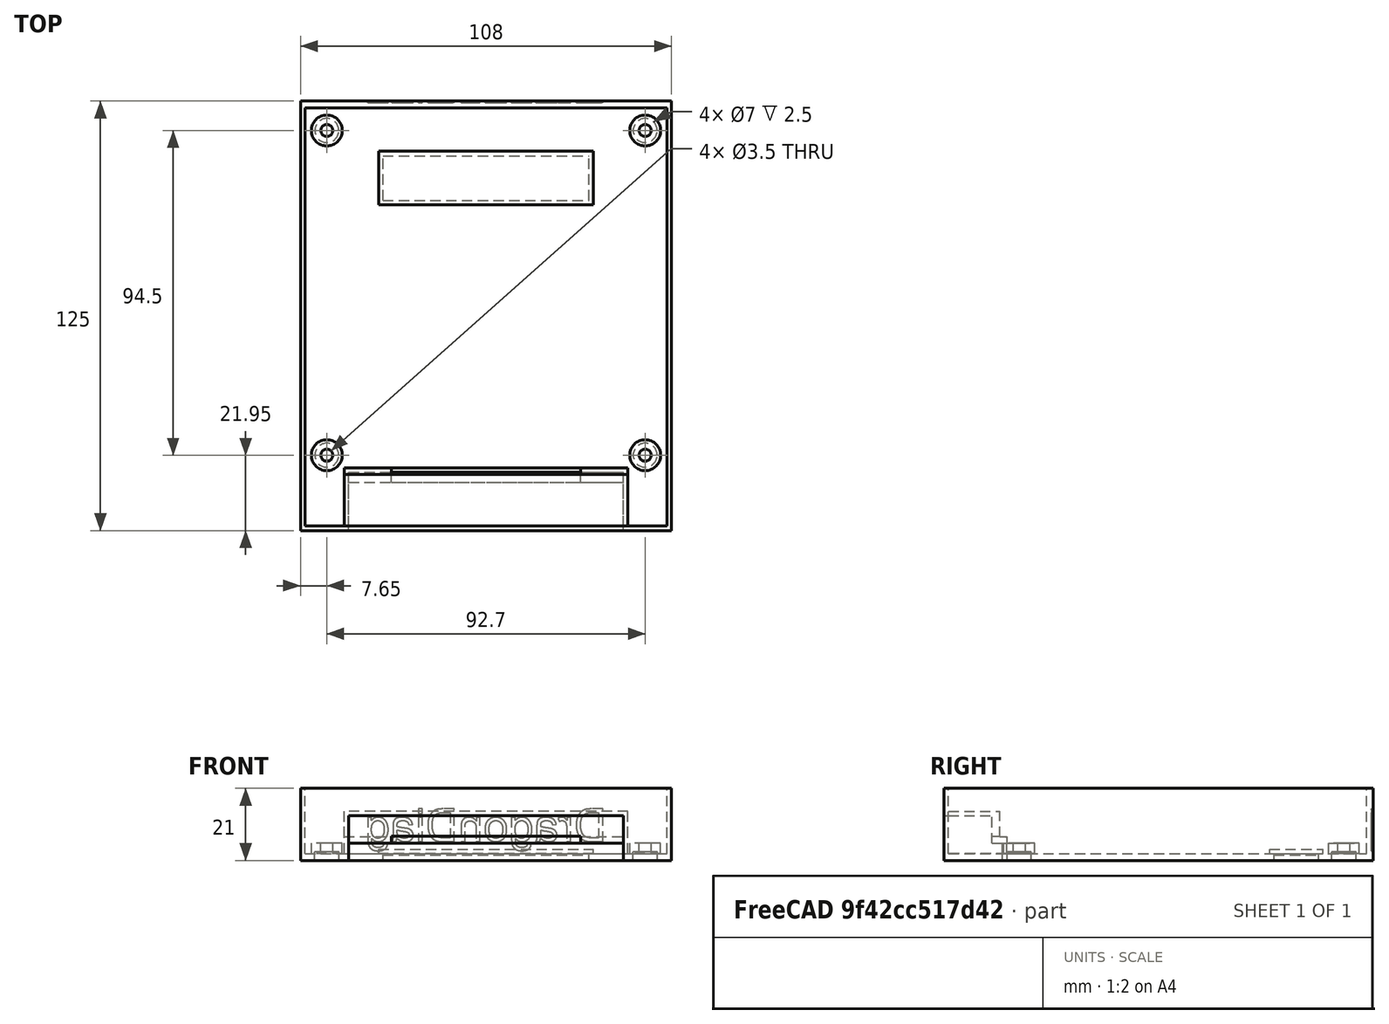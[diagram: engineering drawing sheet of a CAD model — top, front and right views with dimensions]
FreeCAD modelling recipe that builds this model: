
FCSTD DOCUMENT  (FreeCAD 0.18R4 (GitTag))
Label: DragonDiagBottom-v3
License: All rights reserved
LicenseURL: http://en.wikipedia.org/wiki/All_rights_reserved
objects: Part::Box×10, Part::Cut×9, Part::Cylinder×6, Part::MultiFuse×5, Part::FeaturePython×3, Part::Part2DObjectPython×1, Part::Extrusion×1
note: 35 computed .brp shape members not serialized (recipe doc carries the construction recipe); baked Part::Feature solids carry a one-line shape summary decoded from their .brp

FEATURE [Part::Box] Box  label="Cube"
  AttacherType = Attacher::AttachEngine3D
  Height = 21
  Length = 108
  Width = 125
FEATURE [Part::Box] Box001  label="Cube001"
  AttacherType = Attacher::AttachEngine3D
  Height = 19
  Length = 105.4
  Placement = pos=(1.3,1.3,2) rot=(0,0,1;0rad)
  Width = 121.7
FEATURE [Part::Cut] Cut  label="Outer Box"
  Base = -> Box
  Tool = -> Box001
FEATURE [Part::Box] Box002  label="Cube002"
  AttacherType = Attacher::AttachEngine3D
  Height = 13
  Length = 80
  Placement = pos=(14,0,0) rot=(0,0,1;0rad)
  Width = 17
FEATURE [Part::Cut] Cut001  label="Cartridge appature cutout"
  Base = -> Cut
  Tool = -> Box002
FEATURE [Part::Box] Box003  label="Appature"
  AttacherType = Attacher::AttachEngine3D
  Height = 14.3
  Length = 82.6
  Placement = pos=(12.7,0,0) rot=(0,0,1;0rad)
  Width = 18.3
FEATURE [Part::Box] Box004  label="Appature bottom outside carve"
  AttacherType = Attacher::AttachEngine3D
  Height = 5
  Length = 80
  Placement = pos=(14,0,0) rot=(0,0,1;0rad)
  Width = 17
FEATURE [Part::Cut] Cut002  label="AppatureC1"
  Base = -> Box003
  Tool = -> Box004
FEATURE [Part::Box] Box005  label="Appature top outside carve"
  AttacherType = Attacher::AttachEngine3D
  Height = 8
  Length = 80
  Placement = pos=(14,0,5) rot=(0,0,1;0rad)
  Width = 14
FEATURE [Part::Cut] Cut003  label="AppatureC2"
  Base = -> Cut002
  Tool = -> Box005
FEATURE [Part::Box] Box006  label="Appature top inside carve"
  AttacherType = Attacher::AttachEngine3D
  Height = 7.4
  Length = 82.6
  Placement = pos=(12.7,16.3,6.9) rot=(0,0,1;0rad)
  Width = 2
FEATURE [Part::Cut] Cut004  label="AppatureC3"
  Base = -> Cut003
  Tool = -> Box006
FEATURE [Part::Box] Box007  label="Board carve"
  AttacherType = Attacher::AttachEngine3D
  Height = 2
  Length = 55
  Placement = pos=(26.5,14,5) rot=(0,0,1;0rad)
  Width = 4.5
FEATURE [Part::Cut] Cut005  label="AppatureC4"
  Base = -> Cut004
  Tool = -> Box007
FEATURE [Part::Box] Box008  label="Bottom cutout"
  AttacherType = Attacher::AttachEngine3D
  Height = 1.6
  Length = 60
  Placement = pos=(24,96.1,0) rot=(0,0,1;0rad)
  Width = 13
FEATURE [Part::MultiFuse] Fusion  label="Case and appature"
  Shapes = -> [Cut005,Cut001]
FEATURE [Part::Cut] Cut006  label="Case with bottom cutout"
  Base = -> Fusion
  Tool = -> Box008
FEATURE [Part::Box] Box009  label="Bottomcutout cover"
  AttacherType = Attacher::AttachEngine3D
  Height = 1.7
  Length = 62.6
  Placement = pos=(22.7,94.8,1.6) rot=(0,0,1;0rad)
  Width = 15.6
FEATURE [Part::Cylinder] Cylinder  label="Board Post 1"
  Angle = 360
  AttacherType = Attacher::AttachEngine3D
  Height = 5
  Placement = pos=(7.65,21.95,0) rot=(0,0,1;0rad)
  Radius = 4.5
FEATURE [Part::Cylinder] Cylinder001  label="Board Post 2"
  Angle = 360
  AttacherType = Attacher::AttachEngine3D
  Height = 5
  Placement = pos=(100.35,21.95,0) rot=(0,0,1;0rad)
  Radius = 4.5
FEATURE [Part::Cylinder] Cylinder002  label="Board Post 3"
  Angle = 360
  AttacherType = Attacher::AttachEngine3D
  Height = 5
  Placement = pos=(7.65,116.45,0) rot=(0,0,1;0rad)
  Radius = 4.5
FEATURE [Part::Cylinder] Cylinder003  label="Board Post 4"
  Angle = 360
  AttacherType = Attacher::AttachEngine3D
  Height = 5
  Placement = pos=(100.35,116.45,0) rot=(0,0,1;0rad)
  Radius = 4.5
FEATURE [Part::Cylinder] Cylinder005  label="centre hole"
  Angle = 360
  AttacherType = Attacher::AttachEngine3D
  Height = 5
  Placement = pos=(7.65,21.95,0) rot=(0,0,1;0rad)
  Radius = 1.75
FEATURE [Part::Cylinder] Cylinder006  label="Bottom hole"
  Angle = 360
  AttacherType = Attacher::AttachEngine3D
  Height = 2.5
  Placement = pos=(7.65,21.95,0) rot=(0,0,1;0rad)
  Radius = 3.5
FEATURE [Part::MultiFuse] Fusion003  label="Hole1"
  Shapes = -> [Cylinder005,Cylinder006]
FEATURE [Part::FeaturePython] Clone  label="Hole2"  # Draft clone (typed FeaturePython)
  AttacherType = Attacher::AttachEngine3D
  Fuse = false
  Objects = -> [Fusion003]
  Placement = pos=(92.7,0,0) rot=(0,0,1;0rad)
  Scale = (1,1,1)
FEATURE [Part::FeaturePython] Clone001  label="Hole3"  # Draft clone (typed FeaturePython)
  AttacherType = Attacher::AttachEngine3D
  Fuse = false
  Objects = -> [Clone]
  Placement = pos=(0,94.5,0) rot=(0,0,1;0rad)
  Scale = (1,1,1)
FEATURE [Part::FeaturePython] Clone002  label="Hole4"  # Draft clone (typed FeaturePython)
  AttacherType = Attacher::AttachEngine3D
  Fuse = false
  Objects = -> [Clone001]
  Placement = pos=(92.7,94.5,0) rot=(0,0,1;0rad)
  Scale = (1,1,1)
FEATURE [Part::MultiFuse] Fusion004  label="Holes"
  Shapes = -> [Fusion003,Clone002,Clone001,Clone]
FEATURE [Part::MultiFuse] Fusion005  label="Case with mounting posts"
  Shapes = -> [Cut006,Cylinder002,Cylinder003,Cylinder,Cylinder001]
FEATURE [Part::Cut] Cut007  label="Case with mounting posts and holes"
  Base = -> Fusion005
  Tool = -> Fusion004
FEATURE [Part::Part2DObjectPython] ShapeString  # Draft 2D object (typed FeaturePython)
  FontFile = <path>
  Size = 10
  String = DragonDiag
  Tracking = 0
FEATURE [Part::Extrusion] Extrude001  label="Name Text"
  Base = -> ShapeString
  Dir = (0,0,1)
  DirMode = 2
  FaceMakerClass = Part::FaceMakerBullseye
  LengthFwd = 0.5
  LengthRev = 0
  Placement = pos=(89,124.5,5.5) rot=(0,0.707107,0.707107;3.14159rad)
  Solid = true
  Symmetric = false
FEATURE [Part::Cut] Cut008  label="Case plus name cutout"
  Base = -> Cut007
  Tool = -> Extrude001
FEATURE [Part::MultiFuse] Fusion006  label="Case plus all cutouts"
  Shapes = -> [Cut008,Box009]
note: 1 file-system path scrubbed to <path> (originals preserved in the JSON sidecar)
